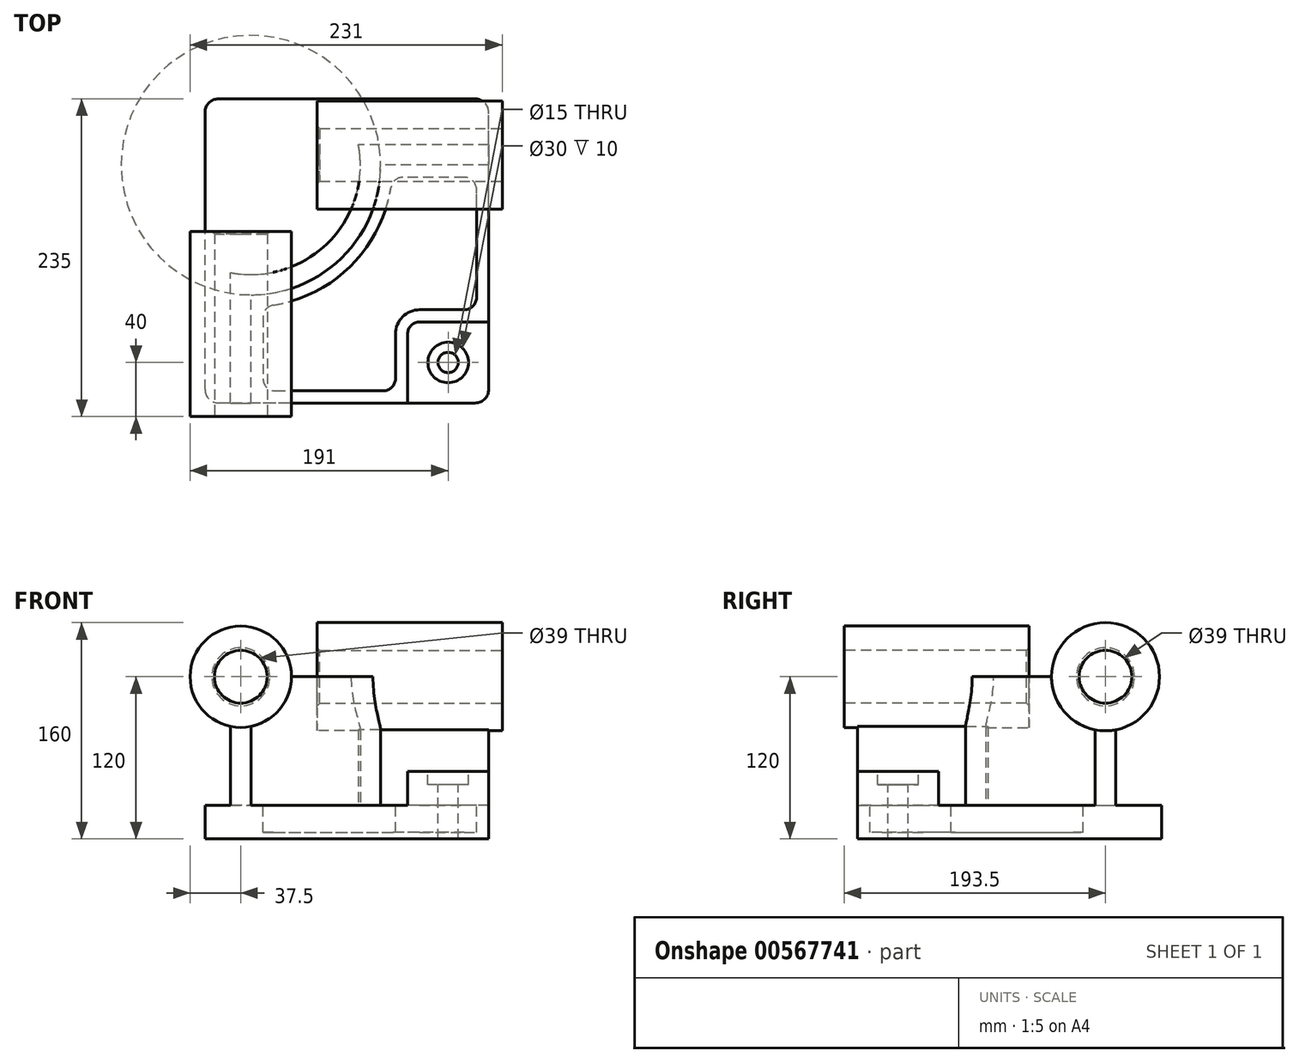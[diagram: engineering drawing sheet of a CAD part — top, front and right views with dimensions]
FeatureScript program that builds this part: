
annotation { "Feature Type Name" : "Feature", "Feature Type Description" : "" }
export const myFeature = defineFeature(function(context is Context, id is Id, definition is map)
    precondition{}
    {
        {
            var Q0;
            Q0=qCreatedBy(makeId("Top.planeOp"),FACE);
            var sketch = newSketch(context, id + "F0", { "sketchPlane" : qUnion([Q0])});
            skLineSegment(sketch, "E0.bottom", {"start": v(105, -112.5) * mm, "end": v(-105, -112.5) * mm});
            skLineSegment(sketch, "E0.top", {"start": v(105, 112.5) * mm, "end": v(-105, 112.5) * mm});
            skLineSegment(sketch, "E0.left", {"start": v(105, -112.5) * mm, "end": v(105, 112.5) * mm});
            skLineSegment(sketch, "E0.right", {"start": v(-105, -112.5) * mm, "end": v(-105, 112.5) * mm});
            skPoint(sketch, "E0.middle", {"position": v(0, 0) * mm});
            skSolve(sketch);
        }
        {
            var Q0;
            Q0=makeQuery(id+"F0.imprint","IMPRINT",FACE,{"disambiguationData":[TD([[makeQuery(id+"F0.imprint","IMPRINT",EDGE,{"derivedFrom":sQuery(id+"F0.wireOp",EDGE,"E0.bottom")}),-1.0]])]});
            extrude(context, id + "F1", {"entities" : qUnion([Q0]), "depth" : 25 * mm, "offsetDistance" : 25 * mm});
        }
        {
            var Q0;
            Q0=makeQuery(id+"F1.opExtrude","CAP_FACE",FACE,{"disambiguationData":[OSD([sQuery(id+"F0.wireOp",EDGE,"E0.bottom"),sQuery(id+"F0.wireOp",EDGE,"E0.top"),sQuery(id+"F0.wireOp",EDGE,"E0.left"),sQuery(id+"F0.wireOp",EDGE,"E0.right")])],"isStart":false});
            var sketch = newSketch(context, id + "F2", { "sketchPlane" : qUnion([Q0])});
            skLineSegment(sketch, "E1", {"start": v(-71, -112.5) * mm, "end": v(-71, -32.5) * mm});
            skLineSegment(sketch, "E2", {"start": v(105, 63.5) * mm, "end": v(25, 63.5) * mm});
            skArc(sketch, "E3", {"start": v(-71, -32.5) * mm, "mid": v(-3.12, -4.38) * mm, "end": v(25, 63.5) * mm});
            skLineSegment(sketch, "E4", {"start": v(-71, -32.5) * mm, "end": v(-71, 63.5) * mm, "construction": true});
            skLineSegment(sketch, "E5", {"start": v(-71, 63.5) * mm, "end": v(25, 63.5) * mm, "construction": true});
            skLineSegment(sketch, "E6.0", {"start": v(-86, -112.5) * mm, "end": v(-86, -16.1) * mm});
            skArc(sketch, "E6.1", {"start": v(-86, -16.1) * mm, "mid": v(-13.72, 6.22) * mm, "end": v(8.6, 78.5) * mm});
            skLineSegment(sketch, "E6.2", {"start": v(105, 78.5) * mm, "end": v(8.6, 78.5) * mm});
            skSolve(sketch);
        }
        {
            var Q0;
            {var subQ4=sQuery(id+"F2.wireOp",EDGE,"E1");Q0=makeQuery(id+"F2.imprint","IMPRINT",FACE,{"disambiguationData":[TD([[makeQuery(id+"F2.imprint","IMPRINT",EDGE,{"derivedFrom":subQ4}),1.0]])]});}
            extrude(context, id + "F3", {"entities" : qUnion([Q0]), "operationType" : NewBodyOperationType.ADD, "depth" : 95 * mm, "offsetDistance" : 25 * mm});
        }
        {
            var Q0;
            {var subQ0=sQuery(id+"F0.wireOp",EDGE,"E0.bottom");Q0=makeQuery(id+"F3.boolean.opBoolean","MERGE",FACE,{"derivedFrom":[makeQuery(id+"F1.opExtrude","SWEPT_FACE",FACE,{"disambiguationData":[OSD([subQ0])]}),makeQuery(id+"F3.opExtrude","SWEPT_FACE",FACE,{"disambiguationData":[OSD([subQ0])]})]});}
            var sketch = newSketch(context, id + "F4", { "sketchPlane" : qUnion([Q0])});
            skCircle(sketch, "E7", {"center": v(-78.5, 120) * mm, "radius": 37.5 * mm});
            skSolve(sketch);
        }
        {
            var Q0;
            {var subQ1=sQuery(id+"F0.wireOp",EDGE,"E0.bottom");var subQ6=makeQuery(id+"F3.opExtrude","CAP_EDGE",EDGE,{"disambiguationData":[OSD([subQ1])],"isStart":false});Q0=makeQuery(id+"F4.imprint","IMPRINT",FACE,{"disambiguationData":[TD([[makeQuery(id+"F4.imprint","IMPRINT",EDGE,{"derivedFrom":subQ6}),1.0]])]});}
            var Q1;
            {var subQ1=sQuery(id+"F0.wireOp",EDGE,"E0.bottom");var subQ6=makeQuery(id+"F3.opExtrude","CAP_EDGE",EDGE,{"disambiguationData":[OSD([subQ1])],"isStart":false});Q1=makeQuery(id+"F4.imprint","IMPRINT",FACE,{"disambiguationData":[TD([[makeQuery(id+"F4.imprint","IMPRINT",EDGE,{"derivedFrom":subQ6}),-1.0]])]});}
            extrude(context, id + "F5", {"entities" : qUnion([Q0, Q1]), "operationType" : NewBodyOperationType.ADD, "depth" : 10 * mm, "offsetDistance" : 25 * mm, "hasSecondDirection" : true, "secondDirectionOppositeDirection" : true, "secondDirectionDepth" : 127 * mm});
        }
        {
            var Q0;
            {var subQ0=sQuery(id+"F0.wireOp",EDGE,"E0.left");Q0=makeQuery(id+"F3.boolean.opBoolean","MERGE",FACE,{"derivedFrom":[makeQuery(id+"F1.opExtrude","SWEPT_FACE",FACE,{"disambiguationData":[OSD([subQ0])]}),makeQuery(id+"F3.opExtrude","SWEPT_FACE",FACE,{"disambiguationData":[OSD([subQ0])]})]});}
            var sketch = newSketch(context, id + "F6", { "sketchPlane" : qUnion([Q0])});
            skCircle(sketch, "E8", {"center": v(71, 120) * mm, "radius": 40 * mm});
            skSolve(sketch);
        }
        {
            var Q0;
            {var subQ1=sQuery(id+"F0.wireOp",EDGE,"E0.left");var subQ6=makeQuery(id+"F3.opExtrude","CAP_EDGE",EDGE,{"disambiguationData":[OSD([subQ1])],"isStart":false});Q0=makeQuery(id+"F6.imprint","IMPRINT",FACE,{"disambiguationData":[TD([[makeQuery(id+"F6.imprint","IMPRINT",EDGE,{"derivedFrom":subQ6}),-1.0]])]});}
            var Q1;
            {var subQ1=sQuery(id+"F0.wireOp",EDGE,"E0.left");var subQ6=makeQuery(id+"F3.opExtrude","CAP_EDGE",EDGE,{"disambiguationData":[OSD([subQ1])],"isStart":false});Q1=makeQuery(id+"F6.imprint","IMPRINT",FACE,{"disambiguationData":[TD([[makeQuery(id+"F6.imprint","IMPRINT",EDGE,{"derivedFrom":subQ6}),1.0]])]});}
            extrude(context, id + "F7", {"entities" : qUnion([Q0, Q1]), "operationType" : NewBodyOperationType.ADD, "depth" : 10 * mm, "offsetDistance" : 25 * mm, "hasSecondDirection" : true, "secondDirectionOppositeDirection" : true, "secondDirectionDepth" : 127 * mm});
        }
        {
            var Q0;
            {var subQ0=sQuery(id+"F0.wireOp",EDGE,"E0.left");var subQ1=sQuery(id+"F0.wireOp",EDGE,"E0.bottom");Q0=makeQuery(id+"F3.boolean.opBoolean","SPLIT",FACE,{"disambiguationData":[TD([makeQuery(id+"F3.opExtrude","SWEPT_FACE",FACE,{"disambiguationData":[OSD([sQuery(id+"F2.wireOp",EDGE,"E1")])]})])],"derivedFrom":makeQuery(id+"F1.opExtrude","CAP_FACE",FACE,{"disambiguationData":[OSD([subQ1,sQuery(id+"F0.wireOp",EDGE,"E0.top"),subQ0,sQuery(id+"F0.wireOp",EDGE,"E0.right")])],"isStart":false})});}
            var sketch = newSketch(context, id + "F8", { "sketchPlane" : qUnion([Q0])});
            skLineSegment(sketch, "E9.bottom", {"start": v(105, -112.5) * mm, "end": v(45, -112.5) * mm});
            skLineSegment(sketch, "E9.top", {"start": v(105, -52.5) * mm, "end": v(45, -52.5) * mm});
            skLineSegment(sketch, "E9.left", {"start": v(105, -112.5) * mm, "end": v(105, -52.5) * mm});
            skLineSegment(sketch, "E9.right", {"start": v(45, -112.5) * mm, "end": v(45, -52.5) * mm});
            skSolve(sketch);
        }
        {
            var Q0;
            Q0=makeQuery(id+"F8.imprint","IMPRINT",FACE,{"disambiguationData":[TD([[makeQuery(id+"F8.imprint","IMPRINT",EDGE,{"derivedFrom":sQuery(id+"F8.wireOp",EDGE,"E9.bottom")}),-1.0]])]});
            extrude(context, id + "F9", {"entities" : qUnion([Q0]), "operationType" : NewBodyOperationType.ADD, "depth" : 25 * mm, "offsetDistance" : 25 * mm});
        }
        {
            var Q0;
            Q0=makeQuery(id+"F9.opExtrude","SWEPT_EDGE",EDGE,{"disambiguationData":[OSD([sQuery(id+"F8.wireOp",EDGE,"E9.top"),sQuery(id+"F8.wireOp",EDGE,"E9.right")])]});
            fillet(context, id + "F10", {"entities" : qUnion([Q0]), "radius" : 9 * mm, "tangentPropagation" : true, "allowEdgeOverflow" : false});
        }
        {
            var Q0;
            {var subQ0=sQuery(id+"F0.wireOp",EDGE,"E0.left");var subQ1=sQuery(id+"F0.wireOp",EDGE,"E0.bottom");Q0=makeQuery(id+"F3.boolean.opBoolean","SPLIT",FACE,{"disambiguationData":[TD([makeQuery(id+"F3.opExtrude","SWEPT_FACE",FACE,{"disambiguationData":[OSD([sQuery(id+"F2.wireOp",EDGE,"E1")])]})])],"derivedFrom":makeQuery(id+"F1.opExtrude","CAP_FACE",FACE,{"disambiguationData":[OSD([subQ1,sQuery(id+"F0.wireOp",EDGE,"E0.top"),subQ0,sQuery(id+"F0.wireOp",EDGE,"E0.right")])],"isStart":false})});}
            var sketch = newSketch(context, id + "F11", { "sketchPlane" : qUnion([Q0])});
            skLineSegment(sketch, "E10.0", {"start": v(-62, -41.11) * mm, "end": v(-62, -103.5) * mm});
            skArc(sketch, "E10.1", {"start": v(33.61, 54.5) * mm, "mid": v(3.25, -10.75) * mm, "end": v(-62, -41.11) * mm});
            skLineSegment(sketch, "E10.2", {"start": v(-62, -103.5) * mm, "end": v(36, -103.5) * mm});
            skLineSegment(sketch, "E10.3", {"start": v(96, 54.5) * mm, "end": v(33.61, 54.5) * mm});
            skLineSegment(sketch, "E10.4", {"start": v(36, -103.5) * mm, "end": v(36, -61.5) * mm});
            skArc(sketch, "E10.5", {"start": v(36, -61.5) * mm, "mid": v(41.27, -48.77) * mm, "end": v(54, -43.5) * mm});
            skLineSegment(sketch, "E10.6", {"start": v(54, -43.5) * mm, "end": v(96, -43.5) * mm});
            skLineSegment(sketch, "E10.7", {"start": v(96, -43.5) * mm, "end": v(96, 54.5) * mm});
            skSolve(sketch);
        }
        {
            var Q0;
            Q0=makeQuery(id+"F11.imprint","IMPRINT",FACE,{"disambiguationData":[TD([[makeQuery(id+"F11.imprint","IMPRINT",EDGE,{"derivedFrom":sQuery(id+"F11.wireOp",EDGE,"E10.0")}),1.0]])]});
            extrude(context, id + "F12", {"entities" : qUnion([Q0]), "operationType" : NewBodyOperationType.REMOVE, "oppositeDirection" : true, "depth" : (25 - 5) * mm, "offsetDistance" : 25 * mm});
        }
        {
            var Q0;
            Q0=makeQuery(id+"F9.opExtrude","CAP_FACE",FACE,{"disambiguationData":[OSD([sQuery(id+"F8.wireOp",EDGE,"E9.bottom"),sQuery(id+"F8.wireOp",EDGE,"E9.top"),sQuery(id+"F8.wireOp",EDGE,"E9.left"),sQuery(id+"F8.wireOp",EDGE,"E9.right")])],"isStart":false});
            var sketch = newSketch(context, id + "F13", { "sketchPlane" : qUnion([Q0])});
            skCircle(sketch, "E11", {"center": v(75, -82.5) * mm, "radius": 15 * mm});
            skPoint(sketch, "E11.centerSnap0", {"position": v(75, -112.5) * mm});
            skSolve(sketch);
        }
        {
            var Q0;
            Q0=sQuery(id+"F13.wireOp",VERTEX,"E11.center");
            var Q1;
            Q1=makeQuery(id+"F1.opExtrude","SWEPT_BODY",BODY,{"disambiguationData":[OSD([sQuery(id+"F0.wireOp",EDGE,"E0.bottom"),sQuery(id+"F0.wireOp",EDGE,"E0.top"),sQuery(id+"F0.wireOp",EDGE,"E0.left"),sQuery(id+"F0.wireOp",EDGE,"E0.right")])]});
            hole(context, id + "F14", {"style" : HoleStyle.C_BORE, "endStyle" : HoleEndStyle.THROUGH, "holeDiameter" : 15 * mm, "cBoreDiameter" : 30 * mm, "cBoreDepth" : 10 * mm, "isTappedThrough" : true, "tappedDepth" : 12 * mm, "tapClearance" : 3, "startFromSketch" : true, "locations" : qUnion([Q0]), "scope" : qUnion([Q1])});
        }
        {
            var Q0;
            Q0=makeQuery(id+"F12.boolean.opBoolean","COPY",EDGE,{"derivedFrom":makeQuery(id+"F12.opExtrude","SWEPT_EDGE",EDGE,{"disambiguationData":[OSD([sQuery(id+"F11.wireOp",EDGE,"E10.1"),sQuery(id+"F11.wireOp",EDGE,"E10.3")])]})});
            var Q1;
            Q1=makeQuery(id+"F12.boolean.opBoolean","COPY",EDGE,{"derivedFrom":makeQuery(id+"F12.opExtrude","SWEPT_EDGE",EDGE,{"disambiguationData":[OSD([sQuery(id+"F11.wireOp",EDGE,"E10.3"),sQuery(id+"F11.wireOp",EDGE,"E10.7")])]})});
            var Q2;
            Q2=makeQuery(id+"F12.boolean.opBoolean","COPY",EDGE,{"derivedFrom":makeQuery(id+"F12.opExtrude","SWEPT_EDGE",EDGE,{"disambiguationData":[OSD([sQuery(id+"F11.wireOp",EDGE,"E10.0"),sQuery(id+"F11.wireOp",EDGE,"E10.1")])]})});
            var Q3;
            Q3=makeQuery(id+"F12.boolean.opBoolean","COPY",EDGE,{"derivedFrom":makeQuery(id+"F12.opExtrude","SWEPT_EDGE",EDGE,{"disambiguationData":[OSD([sQuery(id+"F11.wireOp",EDGE,"E10.0"),sQuery(id+"F11.wireOp",EDGE,"E10.2")])]})});
            var Q4;
            Q4=makeQuery(id+"F12.boolean.opBoolean","COPY",EDGE,{"derivedFrom":makeQuery(id+"F12.opExtrude","SWEPT_EDGE",EDGE,{"disambiguationData":[OSD([sQuery(id+"F11.wireOp",EDGE,"E10.2"),sQuery(id+"F11.wireOp",EDGE,"E10.4")])]})});
            var Q5;
            Q5=makeQuery(id+"F12.boolean.opBoolean","COPY",EDGE,{"derivedFrom":makeQuery(id+"F12.opExtrude","SWEPT_EDGE",EDGE,{"disambiguationData":[OSD([sQuery(id+"F11.wireOp",EDGE,"E10.6"),sQuery(id+"F11.wireOp",EDGE,"E10.7")])]})});
            fillet(context, id + "F15", {"entities" : qUnion([Q0, Q1, Q2, Q3, Q4, Q5]), "radius" : 9 * mm, "tangentPropagation" : true, "allowEdgeOverflow" : false});
        }
        {
            var Q0;
            Q0=makeQuery(id+"F5.opExtrude","CAP_FACE",FACE,{"disambiguationData":[OSD([sQuery(id+"F4.wireOp",EDGE,"E7")])],"isStart":false});
            var sketch = newSketch(context, id + "F16", { "sketchPlane" : qUnion([Q0])});
            skCircle(sketch, "E12", {"center": v(-78.5, 120) * mm, "radius": 19.5 * mm});
            skSolve(sketch);
        }
        {
            var Q0;
            Q0=makeQuery(id+"F16.imprint","IMPRINT",FACE,{"disambiguationData":[TD([[makeQuery(id+"F16.imprint","IMPRINT",EDGE,{"derivedFrom":sQuery(id+"F16.wireOp",EDGE,"E12")}),1.0]])]});
            extrude(context, id + "F17", {"entities" : qUnion([Q0]), "operationType" : NewBodyOperationType.REMOVE, "endBound" : BoundingType.THROUGH_ALL, "oppositeDirection" : true, "depth" : 25 * mm, "offsetDistance" : 25 * mm});
        }
        {
            var Q0;
            Q0=makeQuery(id+"F7.opExtrude","CAP_FACE",FACE,{"disambiguationData":[OSD([sQuery(id+"F6.wireOp",EDGE,"E8")])],"isStart":false});
            var sketch = newSketch(context, id + "F18", { "sketchPlane" : qUnion([Q0])});
            skCircle(sketch, "E13", {"center": v(71, 120) * mm, "radius": 19.5 * mm});
            skSolve(sketch);
        }
        {
            var Q0;
            Q0=makeQuery(id+"F18.imprint","IMPRINT",FACE,{"disambiguationData":[TD([[makeQuery(id+"F18.imprint","IMPRINT",EDGE,{"derivedFrom":sQuery(id+"F18.wireOp",EDGE,"E13")}),1.0]])]});
            extrude(context, id + "F19", {"entities" : qUnion([Q0]), "operationType" : NewBodyOperationType.REMOVE, "endBound" : BoundingType.THROUGH_ALL, "oppositeDirection" : true, "depth" : 25 * mm, "offsetDistance" : 25 * mm});
        }
        {
            var Q0;
            Q0=makeQuery(id+"F17.boolean.opBoolean","COPY",EDGE,{"derivedFrom":makeQuery(id+"F17.opExtrude","CAP_EDGE",EDGE,{"disambiguationData":[OSD([sQuery(id+"F16.wireOp",EDGE,"E12")])],"isStart":true})});
            var Q1;
            Q1=makeQuery(id+"F19.boolean.opBoolean","COPY",EDGE,{"derivedFrom":makeQuery(id+"F19.opExtrude","CAP_EDGE",EDGE,{"disambiguationData":[OSD([sQuery(id+"F18.wireOp",EDGE,"E13")])],"isStart":true})});
            var Q2;
            Q2=makeQuery(id+"F19.boolean.opBoolean","INTERSECT",EDGE,{"derivedFrom":[makeQuery(id+"F7.opExtrude","CAP_FACE",FACE,{"disambiguationData":[OSD([sQuery(id+"F6.wireOp",EDGE,"E8")])],"isStart":true}),makeQuery(id+"F19.opExtrude","SWEPT_FACE",FACE,{"disambiguationData":[OSD([sQuery(id+"F18.wireOp",EDGE,"E13")])]})]});
            var Q3;
            Q3=makeQuery(id+"F17.boolean.opBoolean","INTERSECT",EDGE,{"derivedFrom":[makeQuery(id+"F5.opExtrude","CAP_FACE",FACE,{"disambiguationData":[OSD([sQuery(id+"F4.wireOp",EDGE,"E7")])],"isStart":true}),makeQuery(id+"F17.opExtrude","SWEPT_FACE",FACE,{"disambiguationData":[OSD([sQuery(id+"F16.wireOp",EDGE,"E12")])]})]});
            chamfer(context, id + "F20", {"entities" : qUnion([Q0, Q1, Q2, Q3]), "width" : 2 * mm, "tangentPropagation" : true});
        }
        {
            var Q0;
            Q0=makeQuery(id+"F9.boolean.opBoolean","MERGE",EDGE,{"derivedFrom":[makeQuery(id+"F1.opExtrude","SWEPT_EDGE",EDGE,{"disambiguationData":[OSD([sQuery(id+"F0.wireOp",EDGE,"E0.bottom"),sQuery(id+"F0.wireOp",EDGE,"E0.left")])]}),makeQuery(id+"F9.opExtrude","SWEPT_EDGE",EDGE,{"disambiguationData":[OSD([sQuery(id+"F8.wireOp",EDGE,"E9.bottom"),sQuery(id+"F8.wireOp",EDGE,"E9.left")])]})]});
            var Q1;
            Q1=makeQuery(id+"F1.opExtrude","SWEPT_EDGE",EDGE,{"disambiguationData":[OSD([sQuery(id+"F0.wireOp",EDGE,"E0.top"),sQuery(id+"F0.wireOp",EDGE,"E0.left")])]});
            var Q2;
            Q2=makeQuery(id+"F1.opExtrude","SWEPT_EDGE",EDGE,{"disambiguationData":[OSD([sQuery(id+"F0.wireOp",EDGE,"E0.bottom"),sQuery(id+"F0.wireOp",EDGE,"E0.right")])]});
            var Q3;
            Q3=makeQuery(id+"F1.opExtrude","SWEPT_EDGE",EDGE,{"disambiguationData":[OSD([sQuery(id+"F0.wireOp",EDGE,"E0.top"),sQuery(id+"F0.wireOp",EDGE,"E0.right")])]});
            fillet(context, id + "F21", {"entities" : qUnion([Q0, Q1, Q2, Q3]), "radius" : 10 * mm, "tangentPropagation" : true, "allowEdgeOverflow" : false});
        }
    });
